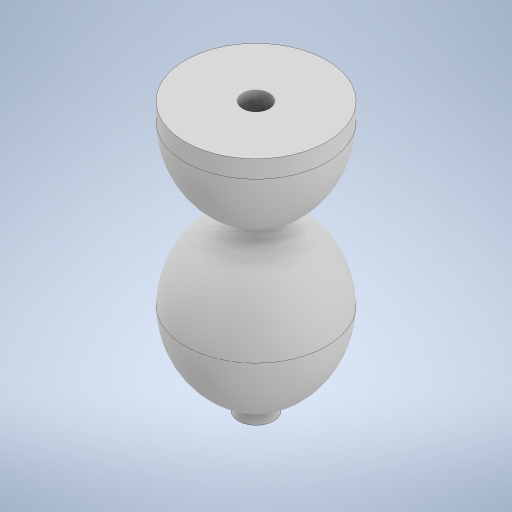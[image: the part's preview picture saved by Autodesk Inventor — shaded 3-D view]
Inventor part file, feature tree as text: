
AUTODESK INVENTOR PART (.ipt)
format: ipt  version: 2023 (Build 270158000, 158)  size: 305,152 bytes
history: native  units: in
note: dims shown in document units (in); Inventor stores cm internally (conversion verified against a paired STEP export)
features: sketch x4, extrude x3, mirror x2, other x1, revolve x1, shell x1
ambient origin geometry x8: Origin, YZ Plane, XZ Plane, XY Plane, X Axis, Y Axis, Z Axis, Center Point
bodies: Body1 (feature_tree)
feature tree (12):
  other  "솔리드1"
  revolve  "회전1"
  mirror  "미러1"
  mirror  "미러2"
  sketch  "스케치2"
  shell  "쉘1"  Thickness=0.1181in
  extrude  "돌출1"  Depth=0.4724in
  extrude  "돌출2"  Depth=0.5315in
  extrude  "돌출3"  Depth=0.5906in
  sketch  "스케치1"
  sketch  "스케치3"
  sketch  "스케치4"
